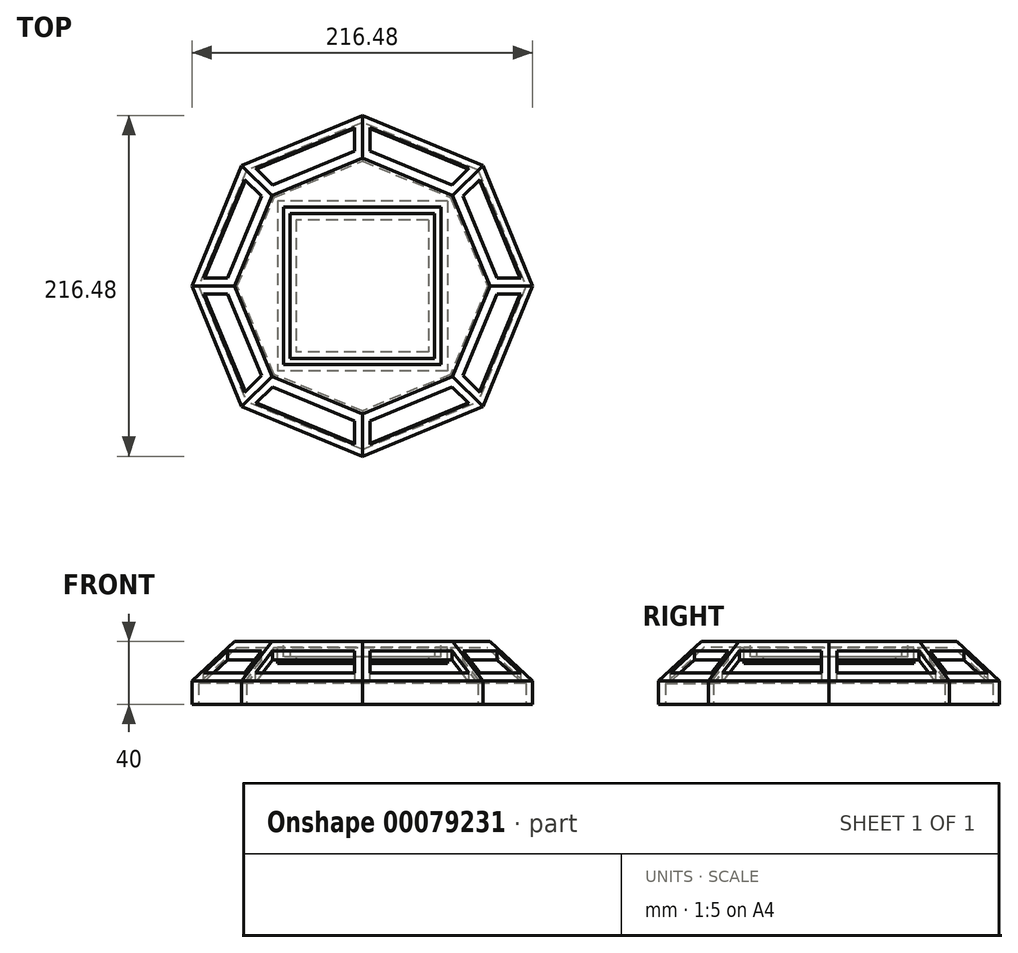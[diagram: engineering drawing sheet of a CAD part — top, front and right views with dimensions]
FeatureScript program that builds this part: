
annotation { "Feature Type Name" : "Feature", "Feature Type Description" : "" }
export const myFeature = defineFeature(function(context is Context, id is Id, definition is map)
    precondition{}
    {
        {
            var Q0;
            Q0=qCreatedBy(makeId("Top.planeOp"),FACE);
            var sketch = newSketch(context, id + "F0", { "sketchPlane" : qUnion([Q0])});
            skCircle(sketch, "E0.cCircle", {"center": v(0, 0) * mm, "radius": 100 * mm, "construction": true});
            skLineSegment(sketch, "E0.0", {"start": v(76.54, 76.54) * mm, "end": v(108.24, 0) * mm});
            skLineSegment(sketch, "E0.1", {"start": v(108.24, 0) * mm, "end": v(76.54, -76.54) * mm});
            skLineSegment(sketch, "E0.2", {"start": v(76.54, -76.54) * mm, "end": v(0, -108.24) * mm});
            skLineSegment(sketch, "E0.3", {"start": v(0, -108.24) * mm, "end": v(-76.54, -76.54) * mm});
            skLineSegment(sketch, "E0.4", {"start": v(-76.54, -76.54) * mm, "end": v(-108.24, 0) * mm});
            skLineSegment(sketch, "E0.5", {"start": v(-108.24, 0) * mm, "end": v(-76.54, 76.54) * mm});
            skLineSegment(sketch, "E0.6", {"start": v(-76.54, 76.54) * mm, "end": v(0, 108.24) * mm});
            skLineSegment(sketch, "E0.7", {"start": v(0, 108.24) * mm, "end": v(76.54, 76.54) * mm});
            skPoint(sketch, "E0.0.midPoint", {"position": v(92.39, 38.27) * mm});
            skSolve(sketch);
        }
        {
            var Q0;
            Q0 = qSketchRegion(id + "F0", true);
            extrude(context, id + "F1", {"entities" : qUnion([Q0]), "depth" : 40 * mm});
        }
        {
            var Q0;
            Q0=makeQuery(id+"F1.opExtrude","CAP_EDGE",EDGE,{"disambiguationData":[OSD([sQuery(id+"F0.wireOp",EDGE,"E0.7")])],"isStart":false});
            var Q1;
            Q1=makeQuery(id+"F1.opExtrude","CAP_EDGE",EDGE,{"disambiguationData":[OSD([sQuery(id+"F0.wireOp",EDGE,"E0.6")])],"isStart":false});
            var Q2;
            Q2=makeQuery(id+"F1.opExtrude","CAP_EDGE",EDGE,{"disambiguationData":[OSD([sQuery(id+"F0.wireOp",EDGE,"E0.5")])],"isStart":false});
            var Q3;
            Q3=makeQuery(id+"F1.opExtrude","CAP_EDGE",EDGE,{"disambiguationData":[OSD([sQuery(id+"F0.wireOp",EDGE,"E0.4")])],"isStart":false});
            var Q4;
            Q4=makeQuery(id+"F1.opExtrude","CAP_EDGE",EDGE,{"disambiguationData":[OSD([sQuery(id+"F0.wireOp",EDGE,"E0.3")])],"isStart":false});
            var Q5;
            Q5=makeQuery(id+"F1.opExtrude","CAP_EDGE",EDGE,{"disambiguationData":[OSD([sQuery(id+"F0.wireOp",EDGE,"E0.2")])],"isStart":false});
            var Q6;
            Q6=makeQuery(id+"F1.opExtrude","CAP_EDGE",EDGE,{"disambiguationData":[OSD([sQuery(id+"F0.wireOp",EDGE,"E0.1")])],"isStart":false});
            var Q7;
            Q7=makeQuery(id+"F1.opExtrude","CAP_EDGE",EDGE,{"disambiguationData":[OSD([sQuery(id+"F0.wireOp",EDGE,"E0.0")])],"isStart":false});
            chamfer(context, id + "F2", {"entities" : qUnion([Q0, Q1, Q2, Q3, Q4, Q5, Q6, Q7]), "width" : 25 * mm, "tangentPropagation" : true});
        }
        {
            var Q0;
            Q0=makeQuery(id+"F1.opExtrude","CAP_FACE",FACE,{"disambiguationData":[OSD([sQuery(id+"F0.wireOp",EDGE,"E0.0"),sQuery(id+"F0.wireOp",EDGE,"E0.1"),sQuery(id+"F0.wireOp",EDGE,"E0.2"),sQuery(id+"F0.wireOp",EDGE,"E0.3"),sQuery(id+"F0.wireOp",EDGE,"E0.4"),sQuery(id+"F0.wireOp",EDGE,"E0.5"),sQuery(id+"F0.wireOp",EDGE,"E0.6"),sQuery(id+"F0.wireOp",EDGE,"E0.7")])],"isStart":false});
            var sketch = newSketch(context, id + "F3", { "sketchPlane" : qUnion([Q0])});
            skPoint(sketch, "E1.middle", {"position": v(0, 0) * mm});
            skLineSegment(sketch, "E2.bottom", {"start": v(50, 50) * mm, "end": v(-50, 50) * mm});
            skLineSegment(sketch, "E2.top", {"start": v(50, -50) * mm, "end": v(-50, -50) * mm});
            skLineSegment(sketch, "E2.left", {"start": v(50, 50) * mm, "end": v(50, -50) * mm});
            skLineSegment(sketch, "E2.right", {"start": v(-50, 50) * mm, "end": v(-50, -50) * mm});
            skSolve(sketch);
        }
        {
            var Q0;
            Q0=makeQuery(id+"F3.imprint","IMPRINT",FACE,{"disambiguationData":[TD([[makeQuery(id+"F3.imprint","IMPRINT",EDGE,{"derivedFrom":sQuery(id+"F3.wireOp",EDGE,"E2.bottom")}),1.0]])]});
            extrude(context, id + "F4", {"entities" : qUnion([Q0]), "operationType" : NewBodyOperationType.REMOVE, "oppositeDirection" : true, "depth" : 10 * mm});
        }
        {
            var Q0;
            Q0=makeQuery(id+"F4.boolean.opBoolean","COPY",FACE,{"derivedFrom":makeQuery(id+"F4.opExtrude","CAP_FACE",FACE,{"disambiguationData":[OSD([sQuery(id+"F3.wireOp",EDGE,"E2.bottom"),sQuery(id+"F3.wireOp",EDGE,"E2.top"),sQuery(id+"F3.wireOp",EDGE,"E2.left"),sQuery(id+"F3.wireOp",EDGE,"E2.right")])],"isStart":false})});
            var sketch = newSketch(context, id + "F5", { "sketchPlane" : qUnion([Q0])});
            skPoint(sketch, "E3.middle", {"position": v(0, 0) * mm});
            skPoint(sketch, "E4.top.start.orphan", {"position": v(46.3, -51.73) * mm});
            skPoint(sketch, "E4.right.end.orphan", {"position": v(-110.27, -71.4) * mm});
            skPoint(sketch, "E4.bottom.start.orphan", {"position": v(110.27, 71.4) * mm});
            skPoint(sketch, "E5.trimOffspring.end.orphan", {"position": v(-46.3, 51.73) * mm});
            skPoint(sketch, "E3.right.end.orphan", {"position": v(0, 0) * mm});
            skPoint(sketch, "E3.right.start.orphan", {"position": v(-961.09, 0) * mm});
            skLineSegment(sketch, "E6.bottom", {"start": v(46, 46) * mm, "end": v(-46, 46) * mm});
            skLineSegment(sketch, "E6.top", {"start": v(46, -46) * mm, "end": v(-46, -46) * mm});
            skLineSegment(sketch, "E6.left", {"start": v(46, 46) * mm, "end": v(46, -46) * mm});
            skLineSegment(sketch, "E6.right", {"start": v(-46, 46) * mm, "end": v(-46, -46) * mm});
            skLineSegment(sketch, "E7", {"start": v(0, 0) * mm, "end": v(0, 0) * mm});
            skSolve(sketch);
        }
        {
            var Q0;
            Q0=makeQuery(id+"F5.imprint","IMPRINT",FACE,{"disambiguationData":[TD([[makeQuery(id+"F5.imprint","IMPRINT",EDGE,{"derivedFrom":sQuery(id+"F5.wireOp",EDGE,"E6.bottom")}),1.0]])]});
            extrude(context, id + "F6", {"entities" : qUnion([Q0]), "operationType" : NewBodyOperationType.ADD, "depth" : 4 * mm});
        }
        {
            var Q0;
            Q0=makeQuery(id+"F1.opExtrude","CAP_FACE",FACE,{"disambiguationData":[OSD([sQuery(id+"F0.wireOp",EDGE,"E0.0"),sQuery(id+"F0.wireOp",EDGE,"E0.1"),sQuery(id+"F0.wireOp",EDGE,"E0.2"),sQuery(id+"F0.wireOp",EDGE,"E0.3"),sQuery(id+"F0.wireOp",EDGE,"E0.4"),sQuery(id+"F0.wireOp",EDGE,"E0.5"),sQuery(id+"F0.wireOp",EDGE,"E0.6"),sQuery(id+"F0.wireOp",EDGE,"E0.7")])],"isStart":true});
            shell(context, id + "F7", {"entities" : qUnion([Q0]), "thickness" : 4 * mm});
        }
        {
            var Q0;
            Q0=makeQuery(id+"F1.opExtrude","CAP_FACE",FACE,{"disambiguationData":[OSD([sQuery(id+"F0.wireOp",EDGE,"E0.0"),sQuery(id+"F0.wireOp",EDGE,"E0.1"),sQuery(id+"F0.wireOp",EDGE,"E0.2"),sQuery(id+"F0.wireOp",EDGE,"E0.3"),sQuery(id+"F0.wireOp",EDGE,"E0.4"),sQuery(id+"F0.wireOp",EDGE,"E0.5"),sQuery(id+"F0.wireOp",EDGE,"E0.6"),sQuery(id+"F0.wireOp",EDGE,"E0.7")])],"isStart":false});
            var sketch = newSketch(context, id + "F8", { "sketchPlane" : qUnion([Q0])});
            skLineSegment(sketch, "E8", {"start": v(0, 0) * mm, "end": v(0, 74.14) * mm, "construction": true});
            skLineSegment(sketch, "E9.2", {"start": v(100.76, -5) * mm, "end": v(74.79, -67.71) * mm});
            skLineSegment(sketch, "E9.3", {"start": v(67.71, -74.79) * mm, "end": v(5, -100.76) * mm});
            skLineSegment(sketch, "E9.4", {"start": v(-5, -100.76) * mm, "end": v(-67.71, -74.79) * mm});
            skLineSegment(sketch, "E9.5", {"start": v(-74.79, -67.71) * mm, "end": v(-100.76, -5) * mm});
            skLineSegment(sketch, "E9.6", {"start": v(-100.76, 5) * mm, "end": v(-74.79, 67.71) * mm});
            skPoint(sketch, "E9.0.midPoint", {"position": v(36.36, 87.77) * mm});
            skLineSegment(sketch, "E10.3", {"start": v(-64.07, -57) * mm, "end": v(-85.6, -5) * mm});
            skLineSegment(sketch, "E10.4", {"start": v(64.07, 57) * mm, "end": v(85.6, 5) * mm});
            skLineSegment(sketch, "E10.5", {"start": v(85.6, -5) * mm, "end": v(64.07, -57) * mm});
            skLineSegment(sketch, "E10.6", {"start": v(57, -64.07) * mm, "end": v(5, -85.6) * mm});
            skLineSegment(sketch, "E10.7", {"start": v(-5, -85.6) * mm, "end": v(-57, -64.07) * mm});
            skLineSegment(sketch, "E11.0", {"start": v(-58.46, 65.54) * mm, "end": v(-67.71, 74.79) * mm});
            skLineSegment(sketch, "E12", {"start": v(-58.46, 65.54) * mm, "end": v(-57, 64.07) * mm});
            skLineSegment(sketch, "E13.0", {"start": v(-65.54, 58.46) * mm, "end": v(-74.79, 67.71) * mm});
            skLineSegment(sketch, "E14", {"start": v(-65.54, 58.46) * mm, "end": v(-64.07, 57) * mm});
            skLineSegment(sketch, "E15", {"start": v(0, 74.14) * mm, "end": v(0, 87.68) * mm, "construction": true});
            skLineSegment(sketch, "E16", {"start": v(0, 0) * mm, "end": v(62, -62) * mm, "construction": true});
            skLineSegment(sketch, "E17.MirrorCS", {"start": v(58.46, 65.54) * mm, "end": v(67.71, 74.79) * mm});
            skLineSegment(sketch, "E18.MirrorCS", {"start": v(58.46, 65.54) * mm, "end": v(57, 64.07) * mm});
            skLineSegment(sketch, "E19.MirrorCS", {"start": v(65.54, 58.46) * mm, "end": v(64.07, 57) * mm});
            skLineSegment(sketch, "E20.MirrorCS", {"start": v(65.54, 58.46) * mm, "end": v(74.79, 67.71) * mm});
            skLineSegment(sketch, "E21.MirrorCS", {"start": v(-65.54, -58.46) * mm, "end": v(-74.79, -67.71) * mm});
            skLineSegment(sketch, "E22.MirrorCS", {"start": v(-58.46, -65.54) * mm, "end": v(-67.71, -74.79) * mm});
            skLineSegment(sketch, "E23.MirrorCS", {"start": v(-58.46, -65.54) * mm, "end": v(-57, -64.07) * mm});
            skLineSegment(sketch, "E24.MirrorCS", {"start": v(-65.54, -58.46) * mm, "end": v(-64.07, -57) * mm});
            skLineSegment(sketch, "E25.MirrorCS", {"start": v(65.54, -58.46) * mm, "end": v(74.79, -67.71) * mm});
            skLineSegment(sketch, "E26.MirrorCS", {"start": v(65.54, -58.46) * mm, "end": v(64.07, -57) * mm});
            skLineSegment(sketch, "E27.MirrorCS", {"start": v(58.46, -65.54) * mm, "end": v(57, -64.07) * mm});
            skLineSegment(sketch, "E28.MirrorCS", {"start": v(58.46, -65.54) * mm, "end": v(67.71, -74.79) * mm});
            skLineSegment(sketch, "E29.MirrorCS", {"start": v(-5, -87.68) * mm, "end": v(-5, -85.6) * mm});
            skLineSegment(sketch, "E30.MirrorCS", {"start": v(5, -87.68) * mm, "end": v(5, -85.6) * mm});
            skLineSegment(sketch, "E31.MirrorCS", {"start": v(5, -87.68) * mm, "end": v(5, -100.76) * mm});
            skLineSegment(sketch, "E32.MirrorCS", {"start": v(-5, -87.68) * mm, "end": v(-5, -100.76) * mm});
            skLineSegment(sketch, "E33.MirrorCS", {"start": v(-5, 87.68) * mm, "end": v(-5, 85.6) * mm});
            skLineSegment(sketch, "E34.MirrorCS", {"start": v(5, 87.68) * mm, "end": v(5, 85.6) * mm});
            skLineSegment(sketch, "E35.MirrorCS", {"start": v(5, 87.68) * mm, "end": v(5, 100.76) * mm});
            skLineSegment(sketch, "E36.MirrorCS", {"start": v(-5, 87.68) * mm, "end": v(-5, 100.76) * mm});
            skLineSegment(sketch, "E37.MirrorCS", {"start": v(87.68, -5) * mm, "end": v(100.76, -5) * mm});
            skLineSegment(sketch, "E38.MirrorCS", {"start": v(87.68, 5) * mm, "end": v(100.76, 5) * mm});
            skLineSegment(sketch, "E39.MirrorCS", {"start": v(87.68, -5) * mm, "end": v(85.6, -5) * mm});
            skLineSegment(sketch, "E40.MirrorCS", {"start": v(87.68, 5) * mm, "end": v(85.6, 5) * mm});
            skLineSegment(sketch, "E41.MirrorCS", {"start": v(-87.68, 5) * mm, "end": v(-85.6, 5) * mm});
            skLineSegment(sketch, "E42.MirrorCS", {"start": v(-87.68, -5) * mm, "end": v(-85.6, -5) * mm});
            skLineSegment(sketch, "E43.MirrorCS", {"start": v(-87.68, -5) * mm, "end": v(-100.76, -5) * mm});
            skLineSegment(sketch, "E44.MirrorCS", {"start": v(-87.68, 5) * mm, "end": v(-100.76, 5) * mm});
            skPoint(sketch, "E45.orphan", {"position": v(72.71, -72.71) * mm});
            skPoint(sketch, "E46.orphan", {"position": v(72.71, 72.71) * mm});
            skPoint(sketch, "E47.orphan", {"position": v(0, 102.83) * mm});
            skPoint(sketch, "E48.orphan", {"position": v(-72.71, 72.71) * mm});
            skPoint(sketch, "E49.orphan", {"position": v(-72.71, -72.71) * mm});
            skPoint(sketch, "E50.orphan", {"position": v(0, -102.83) * mm});
            skLineSegment(sketch, "E51", {"start": v(-64.07, 57) * mm, "end": v(-85.6, 5) * mm});
            skLineSegment(sketch, "E52", {"start": v(5, 100.76) * mm, "end": v(67.71, 74.79) * mm});
            skLineSegment(sketch, "E53", {"start": v(5, 85.6) * mm, "end": v(57, 64.07) * mm});
            skLineSegment(sketch, "E54", {"start": v(-57, 64.07) * mm, "end": v(-5, 85.6) * mm});
            skLineSegment(sketch, "E55", {"start": v(-67.71, 74.79) * mm, "end": v(-5, 100.76) * mm});
            skPoint(sketch, "E56.end.orphan", {"position": v(62, 62) * mm});
            skLineSegment(sketch, "E57", {"start": v(100.76, 5) * mm, "end": v(74.79, 67.71) * mm});
            skPoint(sketch, "E58.end.orphan", {"position": v(-36.36, -87.77) * mm});
            skSolve(sketch);
        }
        {
            var Q0;
            Q0=makeQuery(id+"F8.imprint","IMPRINT",FACE,{"disambiguationData":[TD([[makeQuery(id+"F8.imprint","IMPRINT",EDGE,{"derivedFrom":sQuery(id+"F8.wireOp",EDGE,"E9.4")}),-1.0]])]});
            var Q1;
            Q1=makeQuery(id+"F8.imprint","IMPRINT",FACE,{"disambiguationData":[TD([[makeQuery(id+"F8.imprint","IMPRINT",EDGE,{"derivedFrom":sQuery(id+"F8.wireOp",EDGE,"E9.3")}),-1.0]])]});
            var Q2;
            Q2=makeQuery(id+"F8.imprint","IMPRINT",FACE,{"disambiguationData":[TD([[makeQuery(id+"F8.imprint","IMPRINT",EDGE,{"derivedFrom":sQuery(id+"F8.wireOp",EDGE,"E10.4")}),1.0]])]});
            var Q3;
            Q3=makeQuery(id+"F8.imprint","IMPRINT",FACE,{"disambiguationData":[TD([[makeQuery(id+"F8.imprint","IMPRINT",EDGE,{"derivedFrom":sQuery(id+"F8.wireOp",EDGE,"E17.MirrorCS")}),1.0]])]});
            var Q4;
            Q4=makeQuery(id+"F8.imprint","IMPRINT",FACE,{"disambiguationData":[TD([[makeQuery(id+"F8.imprint","IMPRINT",EDGE,{"derivedFrom":sQuery(id+"F8.wireOp",EDGE,"E11.0")}),-1.0]])]});
            var Q5;
            Q5=makeQuery(id+"F8.imprint","IMPRINT",FACE,{"disambiguationData":[TD([[makeQuery(id+"F8.imprint","IMPRINT",EDGE,{"derivedFrom":sQuery(id+"F8.wireOp",EDGE,"E9.2")}),-1.0]])]});
            var Q6;
            Q6=makeQuery(id+"F8.imprint","IMPRINT",FACE,{"disambiguationData":[TD([[makeQuery(id+"F8.imprint","IMPRINT",EDGE,{"derivedFrom":sQuery(id+"F8.wireOp",EDGE,"E9.6")}),-1.0]])]});
            var Q7;
            Q7=makeQuery(id+"F8.imprint","IMPRINT",FACE,{"disambiguationData":[TD([[makeQuery(id+"F8.imprint","IMPRINT",EDGE,{"derivedFrom":sQuery(id+"F8.wireOp",EDGE,"E9.5")}),-1.0]])]});
            extrude(context, id + "F9", {"entities" : qUnion([Q0, Q1, Q2, Q3, Q4, Q5, Q6, Q7]), "operationType" : NewBodyOperationType.REMOVE, "oppositeDirection" : true, "depth" : 25 * mm});
        }
    });
